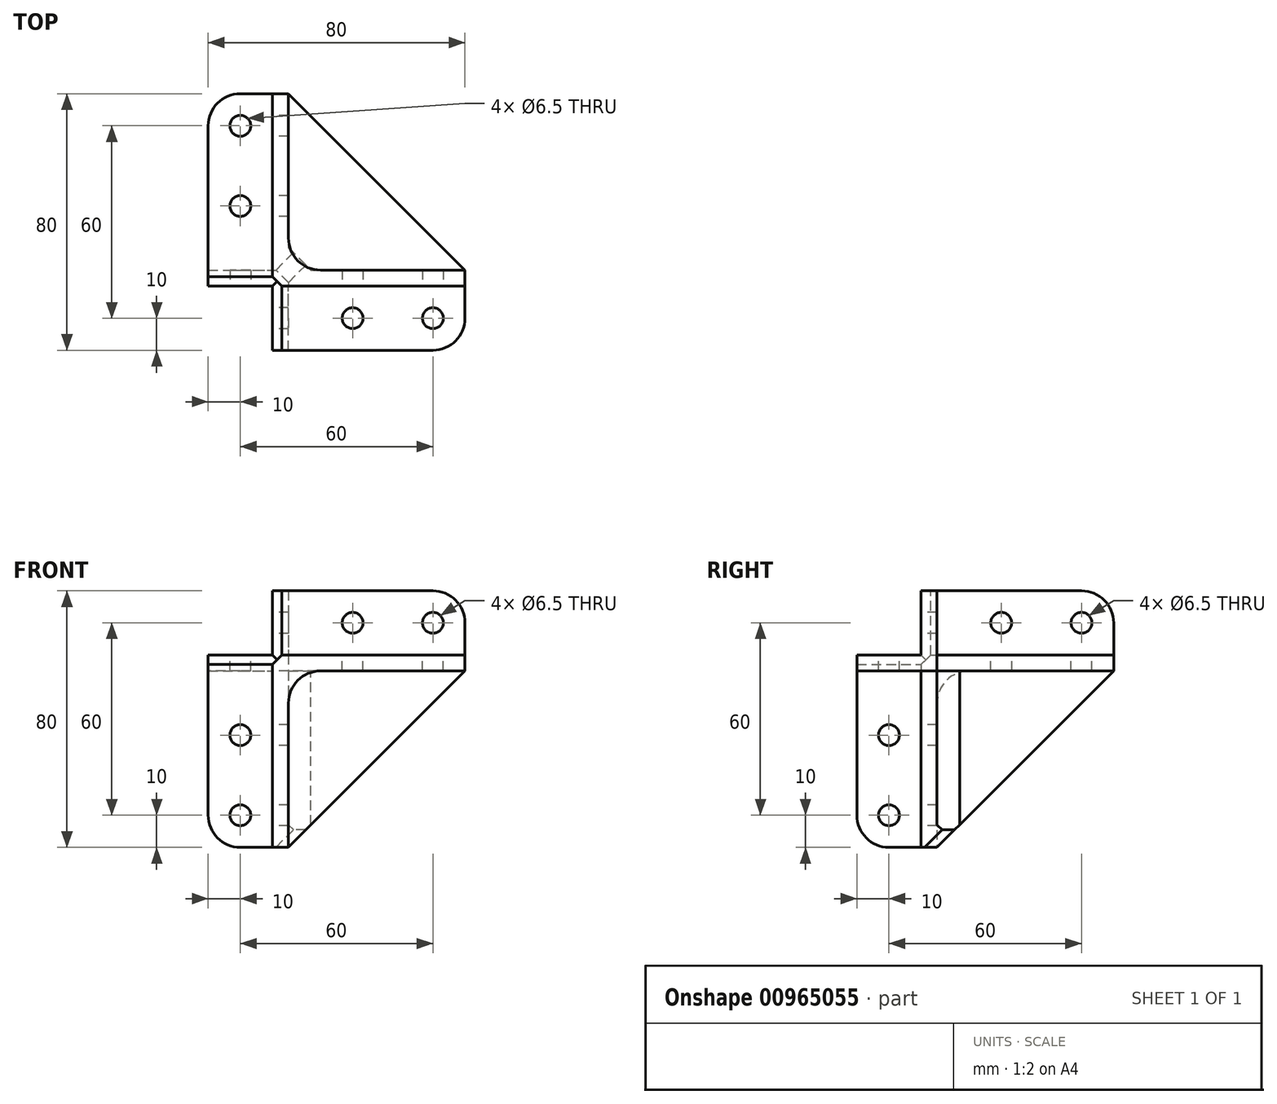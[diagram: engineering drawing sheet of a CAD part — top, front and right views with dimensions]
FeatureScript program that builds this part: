
annotation { "Feature Type Name" : "Feature", "Feature Type Description" : "" }
export const myFeature = defineFeature(function(context is Context, id is Id, definition is map)
    precondition{}
    {
        {
            assignVariable(context, id + "F0", {"variableType" : VariableType.LENGTH, "name" : "s", "lengthValue" : 60 * mm});
        }
        {
            assignVariable(context, id + "F1", {"variableType" : VariableType.LENGTH, "name" : "w", "lengthValue" : 5 * mm});
        }
        {
            var Q0;
            Q0=qCreatedBy(makeId("Top.planeOp"),FACE);
            var sketch = newSketch(context, id + "F2", { "sketchPlane" : qUnion([Q0])});
            skLineSegment(sketch, "E0", {"start": v(0, 0) * mm, "end": v(0, 60) * mm});
            skLineSegment(sketch, "E1", {"start": v(60, 0) * mm, "end": v(0, 0) * mm});
            skLineSegment(sketch, "E2", {"start": v(60, 0) * mm, "end": v(60, 5) * mm});
            skLineSegment(sketch, "E3", {"start": v(60, 5) * mm, "end": v(5, 5) * mm});
            skLineSegment(sketch, "E4", {"start": v(5, 5) * mm, "end": v(5, 60) * mm});
            skLineSegment(sketch, "E5", {"start": v(5, 60) * mm, "end": v(0, 60) * mm});
            skSolve(sketch);
        }
        {
            var Q0;
            Q0=makeQuery(id+"F2.imprint","IMPRINT",FACE,{"disambiguationData":[TD([[makeQuery(id+"F2.imprint","IMPRINT",EDGE,{"derivedFrom":sQuery(id+"F2.wireOp",EDGE,"E0")}),-1.0]])]});
            extrude(context, id + "F3", {"entities" : qUnion([Q0]), "depth" : getVariable(context, 's'), "offsetDistance" : 25 * mm});
        }
        {
            var Q0;
            Q0=makeQuery(id+"F3.opExtrude","SWEPT_FACE",FACE,{"disambiguationData":[OSD([sQuery(id+"F2.wireOp",EDGE,"E4")])]});
            var sketch = newSketch(context, id + "F4", { "sketchPlane" : qUnion([Q0])});
            skLineSegment(sketch, "E6.bottom", {"start": v(60, 60) * mm, "end": v(5, 60) * mm});
            skLineSegment(sketch, "E6.top", {"start": v(60, 55) * mm, "end": v(5, 55) * mm});
            skLineSegment(sketch, "E6.left", {"start": v(60, 60) * mm, "end": v(60, 55) * mm});
            skLineSegment(sketch, "E6.right", {"start": v(5, 60) * mm, "end": v(5, 55) * mm});
            skSolve(sketch);
        }
        {
            var Q0;
            Q0=makeQuery(id+"F4.imprint","IMPRINT",FACE,{"disambiguationData":[TD([[makeQuery(id+"F4.imprint","IMPRINT",EDGE,{"derivedFrom":sQuery(id+"F4.wireOp",EDGE,"E6.bottom")}),-1.0]])]});
            extrude(context, id + "F5", {"entities" : qUnion([Q0]), "operationType" : NewBodyOperationType.ADD, "depth" : getVariable(context, 's') - getVariable(context, 'w'), "offsetDistance" : 25 * mm});
        }
        {
            var Q0;
            Q0=makeQuery(id+"F5.opExtrude","CAP_EDGE",EDGE,{"disambiguationData":[OSD([sQuery(id+"F4.wireOp",EDGE,"E6.left")])],"isStart":false});
            var Q1;
            Q1=makeQuery(id+"F3.opExtrude","CAP_EDGE",EDGE,{"disambiguationData":[OSD([sQuery(id+"F2.wireOp",EDGE,"E2")])],"isStart":true});
            var Q2;
            Q2=makeQuery(id+"F3.opExtrude","CAP_EDGE",EDGE,{"disambiguationData":[OSD([sQuery(id+"F2.wireOp",EDGE,"E5")])],"isStart":true});
            chamfer(context, id + "F6", {"entities" : qUnion([Q0, Q1, Q2]), "width" : 55 * mm, "tangentPropagation" : true});
        }
        {
            var Q0;
            Q0=makeQuery(id+"F3.opExtrude","SWEPT_FACE",FACE,{"disambiguationData":[OSD([sQuery(id+"F2.wireOp",EDGE,"E0")])]});
            var sketch = newSketch(context, id + "F7", { "sketchPlane" : qUnion([Q0])});
            skLineSegment(sketch, "E7.top", {"start": v(-60, 60) * mm, "end": v(0, 60) * mm});
            skLineSegment(sketch, "E7.left", {"start": v(-60, 55) * mm, "end": v(-60, 60) * mm});
            skLineSegment(sketch, "E8", {"start": v(-60, 55) * mm, "end": v(-5, 55) * mm});
            skLineSegment(sketch, "E9", {"start": v(-5, 55) * mm, "end": v(-5, 0) * mm});
            skLineSegment(sketch, "E10", {"start": v(-5, 0) * mm, "end": v(0, 0) * mm});
            skLineSegment(sketch, "E11", {"start": v(0, 0) * mm, "end": v(0, 60) * mm});
            skSolve(sketch);
        }
        {
            var Q0;
            Q0=makeQuery(id+"F3.opExtrude","SWEPT_FACE",FACE,{"disambiguationData":[OSD([sQuery(id+"F2.wireOp",EDGE,"E1")])]});
            var sketch = newSketch(context, id + "F8", { "sketchPlane" : qUnion([Q0])});
            skLineSegment(sketch, "E12", {"start": v(60, 60) * mm, "end": v(60, 55) * mm});
            skLineSegment(sketch, "E13", {"start": v(60, 55) * mm, "end": v(5, 55) * mm});
            skLineSegment(sketch, "E14", {"start": v(5, 55) * mm, "end": v(5, 0) * mm});
            skLineSegment(sketch, "E15", {"start": v(5, 0) * mm, "end": v(0, 0) * mm});
            skLineSegment(sketch, "E16", {"start": v(0, 0) * mm, "end": v(0, 60) * mm});
            skLineSegment(sketch, "E17", {"start": v(0, 60) * mm, "end": v(60, 60) * mm});
            skSolve(sketch);
        }
        {
            var Q0;
            Q0=makeQuery(id+"F5.boolean.opBoolean","MERGE",FACE,{"derivedFrom":[makeQuery(id+"F3.opExtrude","CAP_FACE",FACE,{"disambiguationData":[OSD([sQuery(id+"F2.wireOp",EDGE,"E0"),sQuery(id+"F2.wireOp",EDGE,"E1"),sQuery(id+"F2.wireOp",EDGE,"E2"),sQuery(id+"F2.wireOp",EDGE,"E3"),sQuery(id+"F2.wireOp",EDGE,"E4"),sQuery(id+"F2.wireOp",EDGE,"E5")])],"isStart":false}),makeQuery(id+"F5.opExtrude","SWEPT_FACE",FACE,{"disambiguationData":[OSD([sQuery(id+"F4.wireOp",EDGE,"E6.bottom")])]})]});
            var sketch = newSketch(context, id + "F9", { "sketchPlane" : qUnion([Q0])});
            skLineSegment(sketch, "E18", {"start": v(60, 5) * mm, "end": v(5, 5) * mm});
            skLineSegment(sketch, "E19", {"start": v(5, 5) * mm, "end": v(5, 60) * mm});
            skLineSegment(sketch, "E20", {"start": v(5, 60) * mm, "end": v(0, 60) * mm});
            skLineSegment(sketch, "E21", {"start": v(0, 60) * mm, "end": v(0, 0) * mm});
            skLineSegment(sketch, "E22", {"start": v(0, 0) * mm, "end": v(60, 0) * mm});
            skLineSegment(sketch, "E23", {"start": v(60, 0) * mm, "end": v(60, 5) * mm});
            skPoint(sketch, "E24", {"position": v(0, 0) * mm});
            skSolve(sketch);
        }
        {
            var Q0;
            Q0=makeQuery(id+"F8.imprint","IMPRINT",FACE,{"disambiguationData":[TD([[makeQuery(id+"F8.imprint","IMPRINT",EDGE,{"derivedFrom":sQuery(id+"F8.wireOp",EDGE,"E12")}),-1.0]])]});
            extrude(context, id + "F10", {"entities" : qUnion([Q0]), "operationType" : NewBodyOperationType.ADD, "depth" : 20 * mm, "offsetDistance" : 25 * mm});
        }
        {
            var Q0;
            Q0=makeQuery(id+"F9.imprint","IMPRINT",FACE,{"disambiguationData":[TD([[makeQuery(id+"F9.imprint","IMPRINT",EDGE,{"derivedFrom":sQuery(id+"F9.wireOp",EDGE,"E18")}),1.0]])]});
            extrude(context, id + "F11", {"entities" : qUnion([Q0]), "operationType" : NewBodyOperationType.ADD, "depth" : 20 * mm, "offsetDistance" : 25 * mm});
        }
        {
            var Q0;
            Q0=makeQuery(id+"F7.imprint","IMPRINT",FACE,{"disambiguationData":[TD([[makeQuery(id+"F7.imprint","IMPRINT",EDGE,{"derivedFrom":sQuery(id+"F7.wireOp",EDGE,"E7.top")}),1.0]])]});
            extrude(context, id + "F12", {"entities" : qUnion([Q0]), "operationType" : NewBodyOperationType.ADD, "depth" : 20 * mm, "offsetDistance" : 25 * mm});
        }
        {
            var Q0;
            Q0=makeQuery(id+"F10.opExtrude","CAP_EDGE",EDGE,{"disambiguationData":[OSD([sQuery(id+"F8.wireOp",EDGE,"E12")])],"isStart":false});
            var Q1;
            Q1=makeQuery(id+"F10.opExtrude","CAP_EDGE",EDGE,{"disambiguationData":[OSD([sQuery(id+"F8.wireOp",EDGE,"E15")])],"isStart":false});
            var Q2;
            Q2=makeQuery(id+"F12.opExtrude","CAP_EDGE",EDGE,{"disambiguationData":[OSD([sQuery(id+"F7.wireOp",EDGE,"E10")])],"isStart":false});
            var Q3;
            Q3=makeQuery(id+"F12.opExtrude","CAP_EDGE",EDGE,{"disambiguationData":[OSD([sQuery(id+"F7.wireOp",EDGE,"E7.left")])],"isStart":false});
            var Q4;
            Q4=makeQuery(id+"F11.opExtrude","CAP_EDGE",EDGE,{"disambiguationData":[OSD([sQuery(id+"F9.wireOp",EDGE,"E20")])],"isStart":false});
            var Q5;
            Q5=makeQuery(id+"F11.opExtrude","CAP_EDGE",EDGE,{"disambiguationData":[OSD([sQuery(id+"F9.wireOp",EDGE,"E23")])],"isStart":false});
            var Q6;
            Q6=makeQuery(id+"F10.opExtrude","SWEPT_EDGE",EDGE,{"disambiguationData":[OSD([sQuery(id+"F8.wireOp",EDGE,"E13"),sQuery(id+"F8.wireOp",EDGE,"E14")])]});
            var Q7;
            Q7=makeQuery(id+"F11.opExtrude","SWEPT_EDGE",EDGE,{"disambiguationData":[OSD([sQuery(id+"F9.wireOp",EDGE,"E18"),sQuery(id+"F9.wireOp",EDGE,"E19")])]});
            var Q8;
            Q8=makeQuery(id+"F12.opExtrude","SWEPT_EDGE",EDGE,{"disambiguationData":[OSD([sQuery(id+"F7.wireOp",EDGE,"E8"),sQuery(id+"F7.wireOp",EDGE,"E9")])]});
            fillet(context, id + "F13", {"entities" : qUnion([Q0, Q1, Q2, Q3, Q4, Q5, Q6, Q7, Q8]), "tangentPropagation" : true, "radius" : 10 * mm, "defaultsChanged" : false, "vertexSettings" : [], "allowEdgeOverflow" : false});
        }
        {
            var Q0;
            Q0=makeQuery(id+"F5.opExtrude","SWEPT_EDGE",EDGE,{"disambiguationData":[OSD([sQuery(id+"F2.wireOp",EDGE,"E3"),sQuery(id+"F2.wireOp",EDGE,"E4"),sQuery(id+"F4.wireOp",EDGE,"E6.top"),sQuery(id+"F4.wireOp",EDGE,"E6.right")])]});
            var Q1;
            Q1=makeQuery(id+"F5.opExtrude","CAP_EDGE",EDGE,{"disambiguationData":[OSD([sQuery(id+"F4.wireOp",EDGE,"E6.top")])],"isStart":true});
            var Q2;
            Q2=makeQuery(id+"F3.opExtrude","SWEPT_EDGE",EDGE,{"disambiguationData":[OSD([sQuery(id+"F2.wireOp",EDGE,"E3"),sQuery(id+"F2.wireOp",EDGE,"E4")])]});
            chamfer(context, id + "F14", {"entities" : qUnion([Q0, Q1, Q2]), "width" : 7 * mm, "tangentPropagation" : true});
        }
        {
            var Q0;
            Q0=makeQuery(id+"F10.boolean.opBoolean","MERGE",EDGE,{"derivedFrom":[makeQuery(id+"F3.opExtrude","CAP_EDGE",EDGE,{"disambiguationData":[OSD([sQuery(id+"F2.wireOp",EDGE,"E0")])],"isStart":false}),makeQuery(id+"F10.opExtrude","SWEPT_EDGE",EDGE,{"disambiguationData":[OSD([sQuery(id+"F8.wireOp",EDGE,"E16"),sQuery(id+"F8.wireOp",EDGE,"E17")])]})]});
            chamfer(context, id + "F15", {"entities" : qUnion([Q0]), "width" : 3 * mm, "tangentPropagation" : true});
        }
        {
            var Q0;
            Q0=makeQuery(id+"F11.opExtrude","SWEPT_EDGE",EDGE,{"disambiguationData":[OSD([sQuery(id+"F9.wireOp",EDGE,"E21"),sQuery(id+"F9.wireOp",EDGE,"E22")])]});
            chamfer(context, id + "F16", {"entities" : qUnion([Q0]), "width" : 3 * mm, "tangentPropagation" : true});
        }
        {
            var Q0;
            Q0=makeQuery(id+"F12.opExtrude","SWEPT_EDGE",EDGE,{"disambiguationData":[OSD([sQuery(id+"F7.wireOp",EDGE,"E7.top"),sQuery(id+"F7.wireOp",EDGE,"E11")])]});
            chamfer(context, id + "F17", {"entities" : qUnion([Q0]), "width" : 3 * mm, "tangentPropagation" : true});
        }
        {
            var Q0;
            {var subQ0=sQuery(id+"F9.wireOp",EDGE,"E21");var subQ1=makeQuery(id+"F11.opExtrude","SWEPT_FACE",FACE,{"disambiguationData":[OSD([subQ0])]});var subQ2=sQuery(id+"F9.wireOp",EDGE,"E22");var subQ3=sQuery(id+"F9.wireOp",EDGE,"E20");var subQ4=makeQuery(id+"F10.opExtrude","SWEPT_FACE",FACE,{"disambiguationData":[OSD([sQuery(id+"F8.wireOp",EDGE,"E16")])]});var subQ5=sQuery(id+"F2.wireOp",EDGE,"E0");var subQ6=makeQuery(id+"F3.opExtrude","SWEPT_FACE",FACE,{"disambiguationData":[OSD([subQ5])]});Q0=makeQuery(id+"F12.boolean.opBoolean","SPLIT",FACE,{"disambiguationData":[TD([makeQuery(id+"F11.opExtrude","CAP_FACE",FACE,{"disambiguationData":[OSD([sQuery(id+"F9.wireOp",EDGE,"E18"),sQuery(id+"F9.wireOp",EDGE,"E19"),subQ3,subQ0,subQ2,sQuery(id+"F9.wireOp",EDGE,"E23")])],"isStart":false})])],"derivedFrom":makeQuery(id+"F11.boolean.opBoolean","MERGE",FACE,{"derivedFrom":[makeQuery(id+"F10.boolean.opBoolean","MERGE",FACE,{"derivedFrom":[subQ6,subQ4]}),subQ1]})});}
            var sketch = newSketch(context, id + "F18", { "sketchPlane" : qUnion([Q0])});
            skCircle(sketch, "E25", {"center": v(-50, 70) * mm, "radius": 3.25 * mm});
            skCircle(sketch, "E26", {"center": v(-25, 70) * mm, "radius": 3.25 * mm});
            skSolve(sketch);
        }
        {
            var Q0;
            Q0=makeQuery(id+"F18.imprint","IMPRINT",FACE,{"disambiguationData":[TD([[makeQuery(id+"F18.imprint","IMPRINT",EDGE,{"derivedFrom":sQuery(id+"F18.wireOp",EDGE,"E25")}),1.0]])]});
            var Q1;
            Q1=makeQuery(id+"F18.imprint","IMPRINT",FACE,{"disambiguationData":[TD([[makeQuery(id+"F18.imprint","IMPRINT",EDGE,{"derivedFrom":sQuery(id+"F18.wireOp",EDGE,"E26")}),1.0]])]});
            extrude(context, id + "F19", {"entities" : qUnion([Q0, Q1]), "operationType" : NewBodyOperationType.REMOVE, "oppositeDirection" : true, "depth" : 25 * mm, "offsetDistance" : 25 * mm});
        }
        {
            var Q0;
            {var subQ0=sQuery(id+"F4.wireOp",EDGE,"E6.left");var subQ1=sQuery(id+"F2.wireOp",EDGE,"E5");Q0=makeQuery(id+"F14.opChamfer","TWEAK_EDGE",EDGE,{"derivedFrom":[makeQuery(id+"F6.opChamfer","BLEND_VERTEX",VERTEX,{"blendedFrom":[makeQuery(id+"F3.opExtrude","CAP_EDGE",EDGE,{"disambiguationData":[OSD([subQ1])],"isStart":true}),makeQuery(id+"F5.opExtrude","CAP_EDGE",EDGE,{"disambiguationData":[OSD([subQ0])],"isStart":false}),makeQuery(id+"F5.opExtrude","SWEPT_FACE",FACE,{"disambiguationData":[OSD([sQuery(id+"F4.wireOp",EDGE,"E6.top")])]}),makeQuery(id+"F5.boolean.opBoolean","MERGE",FACE,{"derivedFrom":[makeQuery(id+"F3.opExtrude","SWEPT_FACE",FACE,{"disambiguationData":[OSD([subQ1])]}),makeQuery(id+"F5.opExtrude","SWEPT_FACE",FACE,{"disambiguationData":[OSD([subQ0])]})]}),makeQuery(id+"F3.opExtrude","SWEPT_FACE",FACE,{"disambiguationData":[OSD([sQuery(id+"F2.wireOp",EDGE,"E4")])]})],"blendedInto":[makeQuery(id+"F5.opExtrude","SWEPT_FACE",FACE,{"disambiguationData":[OSD([sQuery(id+"F4.wireOp",EDGE,"E6.top")])]}),makeQuery(id+"F5.boolean.opBoolean","MERGE",FACE,{"derivedFrom":[makeQuery(id+"F3.opExtrude","SWEPT_FACE",FACE,{"disambiguationData":[OSD([subQ1])]}),makeQuery(id+"F5.opExtrude","SWEPT_FACE",FACE,{"disambiguationData":[OSD([subQ0])]})]}),makeQuery(id+"F3.opExtrude","SWEPT_FACE",FACE,{"disambiguationData":[OSD([sQuery(id+"F2.wireOp",EDGE,"E4")])]})]})]});}
            var Q1;
            {var subQ0=sQuery(id+"F2.wireOp",EDGE,"E4");var subQ1=sQuery(id+"F2.wireOp",EDGE,"E3");var subQ2=sQuery(id+"F2.wireOp",EDGE,"E5");var subQ3=sQuery(id+"F2.wireOp",EDGE,"E2");Q1=makeQuery(id+"F14.opChamfer","TWEAK_EDGE",EDGE,{"derivedFrom":[makeQuery(id+"F6.opChamfer","BLEND_VERTEX",VERTEX,{"blendedFrom":[makeQuery(id+"F3.opExtrude","CAP_EDGE",EDGE,{"disambiguationData":[OSD([subQ3])],"isStart":true}),makeQuery(id+"F3.opExtrude","CAP_EDGE",EDGE,{"disambiguationData":[OSD([subQ2])],"isStart":true}),makeQuery(id+"F3.opExtrude","CAP_FACE",FACE,{"disambiguationData":[OSD([sQuery(id+"F2.wireOp",EDGE,"E0"),sQuery(id+"F2.wireOp",EDGE,"E1"),subQ3,subQ1,subQ0,subQ2])],"isStart":true}),makeQuery(id+"F3.opExtrude","SWEPT_FACE",FACE,{"disambiguationData":[OSD([subQ1])]}),makeQuery(id+"F3.opExtrude","SWEPT_FACE",FACE,{"disambiguationData":[OSD([subQ0])]})],"blendedInto":[makeQuery(id+"F3.opExtrude","CAP_FACE",FACE,{"disambiguationData":[OSD([sQuery(id+"F2.wireOp",EDGE,"E0"),sQuery(id+"F2.wireOp",EDGE,"E1"),subQ3,subQ1,subQ0,subQ2])],"isStart":true}),makeQuery(id+"F3.opExtrude","SWEPT_FACE",FACE,{"disambiguationData":[OSD([subQ1])]}),makeQuery(id+"F3.opExtrude","SWEPT_FACE",FACE,{"disambiguationData":[OSD([subQ0])]})]})]});}
            var Q2;
            {var subQ0=sQuery(id+"F4.wireOp",EDGE,"E6.left");var subQ1=sQuery(id+"F4.wireOp",EDGE,"E6.top");var subQ2=sQuery(id+"F2.wireOp",EDGE,"E2");Q2=makeQuery(id+"F14.opChamfer","TWEAK_EDGE",EDGE,{"derivedFrom":[makeQuery(id+"F6.opChamfer","BLEND_VERTEX",VERTEX,{"blendedFrom":[makeQuery(id+"F3.opExtrude","CAP_EDGE",EDGE,{"disambiguationData":[OSD([subQ2])],"isStart":true}),makeQuery(id+"F5.opExtrude","CAP_EDGE",EDGE,{"disambiguationData":[OSD([subQ0])],"isStart":false}),makeQuery(id+"F5.opExtrude","SWEPT_FACE",FACE,{"disambiguationData":[OSD([subQ1])]}),makeQuery(id+"F5.boolean.opBoolean","MERGE",FACE,{"derivedFrom":[makeQuery(id+"F3.opExtrude","SWEPT_FACE",FACE,{"disambiguationData":[OSD([subQ2])]}),makeQuery(id+"F5.opExtrude","CAP_FACE",FACE,{"disambiguationData":[OSD([sQuery(id+"F4.wireOp",EDGE,"E6.bottom"),subQ1,subQ0,sQuery(id+"F4.wireOp",EDGE,"E6.right")])],"isStart":false})]}),makeQuery(id+"F3.opExtrude","SWEPT_FACE",FACE,{"disambiguationData":[OSD([sQuery(id+"F2.wireOp",EDGE,"E3")])]})],"blendedInto":[makeQuery(id+"F5.opExtrude","SWEPT_FACE",FACE,{"disambiguationData":[OSD([subQ1])]}),makeQuery(id+"F5.boolean.opBoolean","MERGE",FACE,{"derivedFrom":[makeQuery(id+"F3.opExtrude","SWEPT_FACE",FACE,{"disambiguationData":[OSD([subQ2])]}),makeQuery(id+"F5.opExtrude","CAP_FACE",FACE,{"disambiguationData":[OSD([sQuery(id+"F4.wireOp",EDGE,"E6.bottom"),subQ1,subQ0,sQuery(id+"F4.wireOp",EDGE,"E6.right")])],"isStart":false})]}),makeQuery(id+"F3.opExtrude","SWEPT_FACE",FACE,{"disambiguationData":[OSD([sQuery(id+"F2.wireOp",EDGE,"E3")])]})]})]});}
            chamfer(context, id + "F20", {"entities" : qUnion([Q0, Q1, Q2]), "width" : 5.5 * mm, "tangentPropagation" : true});
        }
        {
            var Q0;
            Q0=makeQuery(id+"F12.opExtrude","SWEPT_FACE",FACE,{"disambiguationData":[OSD([sQuery(id+"F7.wireOp",EDGE,"E7.top")])]});
            var sketch = newSketch(context, id + "F21", { "sketchPlane" : qUnion([Q0])});
            skCircle(sketch, "E27", {"center": v(-10, 25) * mm, "radius": 3.25 * mm});
            skCircle(sketch, "E28", {"center": v(-10, 50) * mm, "radius": 3.25 * mm});
            skSolve(sketch);
        }
        {
            var Q0;
            Q0=makeQuery(id+"F21.imprint","IMPRINT",FACE,{"disambiguationData":[TD([[makeQuery(id+"F21.imprint","IMPRINT",EDGE,{"derivedFrom":sQuery(id+"F21.wireOp",EDGE,"E27")}),1.0]])]});
            var Q1;
            Q1=makeQuery(id+"F21.imprint","IMPRINT",FACE,{"disambiguationData":[TD([[makeQuery(id+"F21.imprint","IMPRINT",EDGE,{"derivedFrom":sQuery(id+"F21.wireOp",EDGE,"E28")}),1.0]])]});
            extrude(context, id + "F22", {"entities" : qUnion([Q0, Q1]), "operationType" : NewBodyOperationType.REMOVE, "oppositeDirection" : true, "depth" : 25 * mm, "offsetDistance" : 25 * mm});
        }
        {
            var Q0;
            Q0=makeQuery(id+"F16.opChamfer","SPLIT",FACE,{"disambiguationData":[OD(0.0)],"derivedFrom":makeQuery(id+"F15.opChamfer","MERGE",FACE,{"derivedFrom":[makeQuery(id+"F11.opExtrude","SWEPT_FACE",FACE,{"disambiguationData":[OSD([sQuery(id+"F9.wireOp",EDGE,"E22")])]}),makeQuery(id+"F12.opExtrude","SWEPT_FACE",FACE,{"disambiguationData":[OSD([sQuery(id+"F7.wireOp",EDGE,"E11")])]})]})});
            var sketch = newSketch(context, id + "F23", { "sketchPlane" : qUnion([Q0])});
            skCircle(sketch, "E29", {"center": v(25, 70) * mm, "radius": 3.25 * mm});
            skCircle(sketch, "E30", {"center": v(50, 70) * mm, "radius": 3.25 * mm});
            skSolve(sketch);
        }
        {
            var Q0;
            Q0=makeQuery(id+"F23.imprint","IMPRINT",FACE,{"disambiguationData":[TD([[makeQuery(id+"F23.imprint","IMPRINT",EDGE,{"derivedFrom":sQuery(id+"F23.wireOp",EDGE,"E29")}),1.0]])]});
            var Q1;
            Q1=makeQuery(id+"F23.imprint","IMPRINT",FACE,{"disambiguationData":[TD([[makeQuery(id+"F23.imprint","IMPRINT",EDGE,{"derivedFrom":sQuery(id+"F23.wireOp",EDGE,"E30")}),1.0]])]});
            extrude(context, id + "F24", {"entities" : qUnion([Q0, Q1]), "operationType" : NewBodyOperationType.REMOVE, "oppositeDirection" : true, "depth" : 25 * mm, "offsetDistance" : 25 * mm});
        }
        {
            var Q0;
            {var subQ1=sQuery(id+"F2.wireOp",EDGE,"E2");var subQ2=sQuery(id+"F4.wireOp",EDGE,"E6.bottom");var subQ3=sQuery(id+"F2.wireOp",EDGE,"E0");var subQ4=sQuery(id+"F8.wireOp",EDGE,"E17");Q0=makeQuery(id+"F11.boolean.opBoolean","SPLIT",FACE,{"disambiguationData":[TD([makeQuery(id+"F3.opExtrude","SWEPT_FACE",FACE,{"disambiguationData":[OSD([subQ3])]})])],"derivedFrom":makeQuery(id+"F10.boolean.opBoolean","MERGE",FACE,{"derivedFrom":[makeQuery(id+"F5.boolean.opBoolean","MERGE",FACE,{"derivedFrom":[makeQuery(id+"F3.opExtrude","CAP_FACE",FACE,{"disambiguationData":[OSD([subQ3,sQuery(id+"F2.wireOp",EDGE,"E1"),subQ1,sQuery(id+"F2.wireOp",EDGE,"E3"),sQuery(id+"F2.wireOp",EDGE,"E4"),sQuery(id+"F2.wireOp",EDGE,"E5")])],"isStart":false}),makeQuery(id+"F5.opExtrude","SWEPT_FACE",FACE,{"disambiguationData":[OSD([subQ2])]})]}),makeQuery(id+"F10.opExtrude","SWEPT_FACE",FACE,{"disambiguationData":[OSD([subQ4])]})]})});}
            var sketch = newSketch(context, id + "F25", { "sketchPlane" : qUnion([Q0])});
            skCircle(sketch, "E31", {"center": v(25, -10) * mm, "radius": 3.25 * mm});
            skCircle(sketch, "E32", {"center": v(50, -10) * mm, "radius": 3.25 * mm});
            skSolve(sketch);
        }
        {
            var Q0;
            Q0=makeQuery(id+"F25.imprint","IMPRINT",FACE,{"disambiguationData":[TD([[makeQuery(id+"F25.imprint","IMPRINT",EDGE,{"derivedFrom":sQuery(id+"F25.wireOp",EDGE,"E31")}),1.0]])]});
            var Q1;
            Q1=makeQuery(id+"F25.imprint","IMPRINT",FACE,{"disambiguationData":[TD([[makeQuery(id+"F25.imprint","IMPRINT",EDGE,{"derivedFrom":sQuery(id+"F25.wireOp",EDGE,"E32")}),1.0]])]});
            extrude(context, id + "F26", {"entities" : qUnion([Q0, Q1]), "operationType" : NewBodyOperationType.REMOVE, "oppositeDirection" : true, "depth" : 25 * mm, "offsetDistance" : 25 * mm});
        }
        {
            var Q0;
            {var subQ0=sQuery(id+"F8.wireOp",EDGE,"E16");var subQ1=makeQuery(id+"F10.opExtrude","SWEPT_FACE",FACE,{"disambiguationData":[OSD([subQ0])]});var subQ2=sQuery(id+"F8.wireOp",EDGE,"E15");var subQ3=makeQuery(id+"F11.opExtrude","SWEPT_FACE",FACE,{"disambiguationData":[OSD([sQuery(id+"F9.wireOp",EDGE,"E21")])]});var subQ4=sQuery(id+"F8.wireOp",EDGE,"E17");var subQ5=sQuery(id+"F2.wireOp",EDGE,"E0");var subQ6=makeQuery(id+"F3.opExtrude","SWEPT_FACE",FACE,{"disambiguationData":[OSD([subQ5])]});Q0=makeQuery(id+"F12.boolean.opBoolean","SPLIT",FACE,{"disambiguationData":[TD([makeQuery(id+"F10.opExtrude","CAP_FACE",FACE,{"disambiguationData":[OSD([sQuery(id+"F8.wireOp",EDGE,"E12"),sQuery(id+"F8.wireOp",EDGE,"E13"),sQuery(id+"F8.wireOp",EDGE,"E14"),subQ2,subQ0,subQ4])],"isStart":false})])],"derivedFrom":makeQuery(id+"F11.boolean.opBoolean","MERGE",FACE,{"derivedFrom":[makeQuery(id+"F10.boolean.opBoolean","MERGE",FACE,{"derivedFrom":[subQ6,subQ1]}),subQ3]})});}
            var sketch = newSketch(context, id + "F27", { "sketchPlane" : qUnion([Q0])});
            skCircle(sketch, "E33", {"center": v(10, 35) * mm, "radius": 3.25 * mm});
            skCircle(sketch, "E34", {"center": v(10, 10) * mm, "radius": 3.25 * mm});
            skSolve(sketch);
        }
        {
            var Q0;
            Q0=makeQuery(id+"F27.imprint","IMPRINT",FACE,{"disambiguationData":[TD([[makeQuery(id+"F27.imprint","IMPRINT",EDGE,{"derivedFrom":sQuery(id+"F27.wireOp",EDGE,"E33")}),1.0]])]});
            var Q1;
            Q1=makeQuery(id+"F27.imprint","IMPRINT",FACE,{"disambiguationData":[TD([[makeQuery(id+"F27.imprint","IMPRINT",EDGE,{"derivedFrom":sQuery(id+"F27.wireOp",EDGE,"E34")}),1.0]])]});
            extrude(context, id + "F28", {"entities" : qUnion([Q0, Q1]), "operationType" : NewBodyOperationType.REMOVE, "oppositeDirection" : true, "depth" : 25 * mm, "offsetDistance" : 25 * mm});
        }
        {
            var Q0;
            Q0=makeQuery(id+"F16.opChamfer","SPLIT",FACE,{"disambiguationData":[OD(1.0)],"derivedFrom":makeQuery(id+"F15.opChamfer","MERGE",FACE,{"derivedFrom":[makeQuery(id+"F11.opExtrude","SWEPT_FACE",FACE,{"disambiguationData":[OSD([sQuery(id+"F9.wireOp",EDGE,"E22")])]}),makeQuery(id+"F12.opExtrude","SWEPT_FACE",FACE,{"disambiguationData":[OSD([sQuery(id+"F7.wireOp",EDGE,"E11")])]})]})});
            var sketch = newSketch(context, id + "F29", { "sketchPlane" : qUnion([Q0])});
            skCircle(sketch, "E35", {"center": v(-10, 35) * mm, "radius": 3.25 * mm});
            skCircle(sketch, "E36", {"center": v(-10, 10) * mm, "radius": 3.25 * mm});
            skSolve(sketch);
        }
        {
            var Q0;
            Q0=makeQuery(id+"F29.imprint","IMPRINT",FACE,{"disambiguationData":[TD([[makeQuery(id+"F29.imprint","IMPRINT",EDGE,{"derivedFrom":sQuery(id+"F29.wireOp",EDGE,"E35")}),1.0]])]});
            var Q1;
            Q1=makeQuery(id+"F29.imprint","IMPRINT",FACE,{"disambiguationData":[TD([[makeQuery(id+"F29.imprint","IMPRINT",EDGE,{"derivedFrom":sQuery(id+"F29.wireOp",EDGE,"E36")}),1.0]])]});
            extrude(context, id + "F30", {"entities" : qUnion([Q0, Q1]), "operationType" : NewBodyOperationType.REMOVE, "oppositeDirection" : true, "depth" : 25 * mm, "offsetDistance" : 25 * mm});
        }
    });
